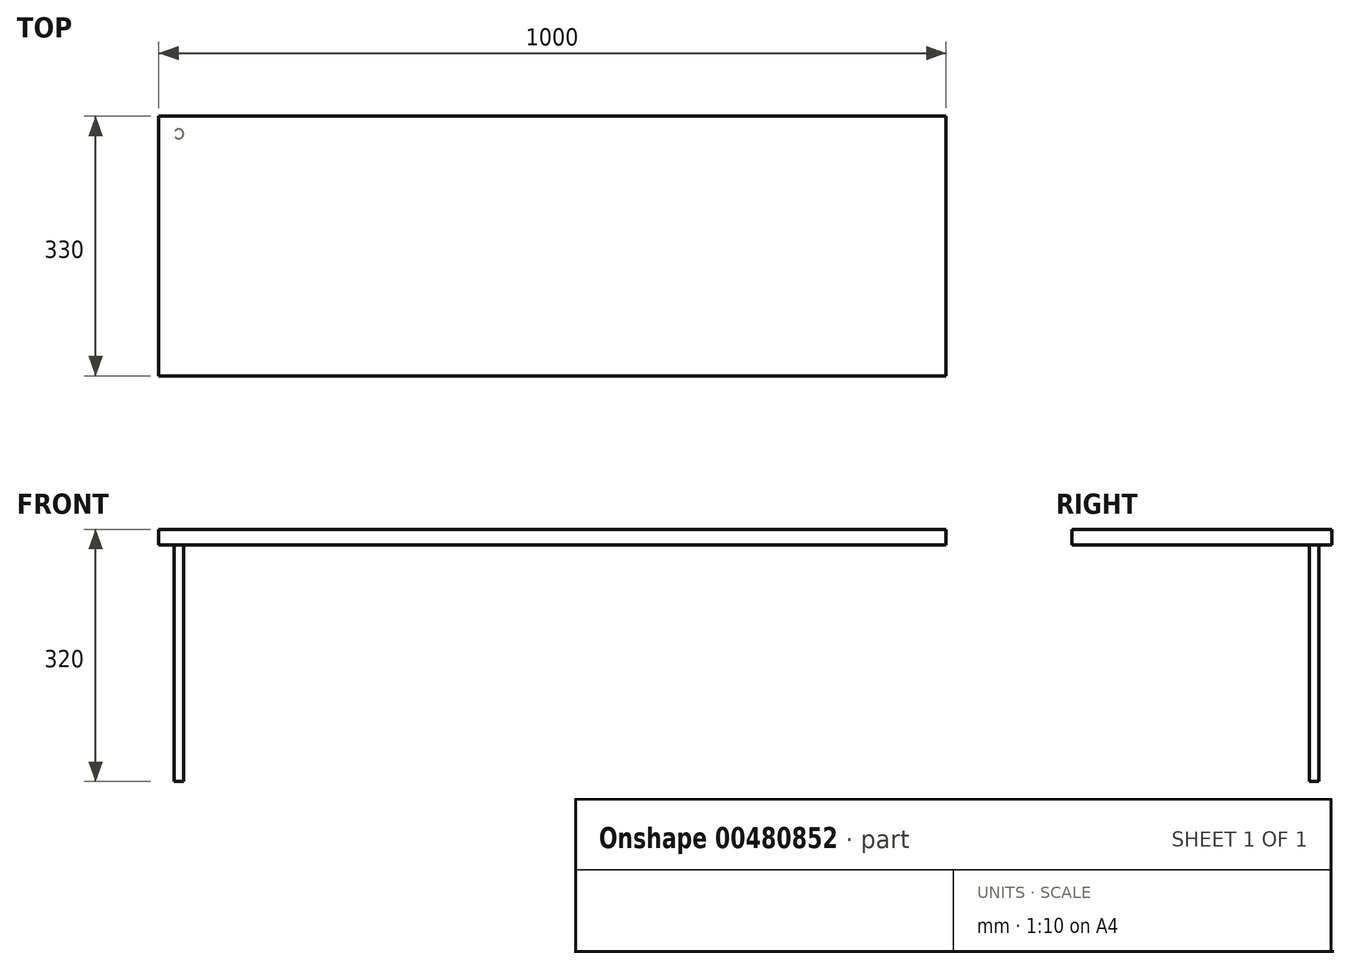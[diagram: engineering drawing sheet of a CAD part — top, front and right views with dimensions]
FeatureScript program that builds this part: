
annotation { "Feature Type Name" : "Feature", "Feature Type Description" : "" }
export const myFeature = defineFeature(function(context is Context, id is Id, definition is map)
    precondition{}
    {
        {
            var Q0;
            Q0=qCreatedBy(makeId("Top.planeOp"),FACE);
            var sketch = newSketch(context, id + "F0", { "sketchPlane" : qUnion([Q0])});
            skLineSegment(sketch, "E0.bottom", {"start": v(-500.02, 164.87) * mm, "end": v(499.98, 164.87) * mm});
            skLineSegment(sketch, "E0.top", {"start": v(-500.02, -165.13) * mm, "end": v(499.98, -165.13) * mm});
            skLineSegment(sketch, "E0.left", {"start": v(-500.02, 164.87) * mm, "end": v(-500.02, -165.13) * mm});
            skLineSegment(sketch, "E0.right", {"start": v(499.98, 164.87) * mm, "end": v(499.98, -165.13) * mm});
            skSolve(sketch);
        }
        {
            var Q0;
            Q0 = qSketchRegion(id + "F0", true);
            extrude(context, id + "F1", {"entities" : qUnion([Q0]), "depth" : 20 * mm});
        }
        {
            var Q0;
            Q0=makeQuery(id+"F1.opExtrude","CAP_FACE",FACE,{"disambiguationData":[OSD([sQuery(id+"F0.wireOp",EDGE,"E0.bottom"),sQuery(id+"F0.wireOp",EDGE,"E0.top"),sQuery(id+"F0.wireOp",EDGE,"E0.left"),sQuery(id+"F0.wireOp",EDGE,"E0.right")])],"isStart":true});
            var sketch = newSketch(context, id + "F2", { "sketchPlane" : qUnion([Q0])});
            skCircle(sketch, "E1", {"center": v(-474.6, -142.39) * mm, "radius": 6 * mm});
            skSolve(sketch);
        }
        {
            var Q0;
            Q0 = qSketchRegion(id + "F2", true);
            extrude(context, id + "F3", {"entities" : qUnion([Q0]), "depth" : 300 * mm});
        }
    });
